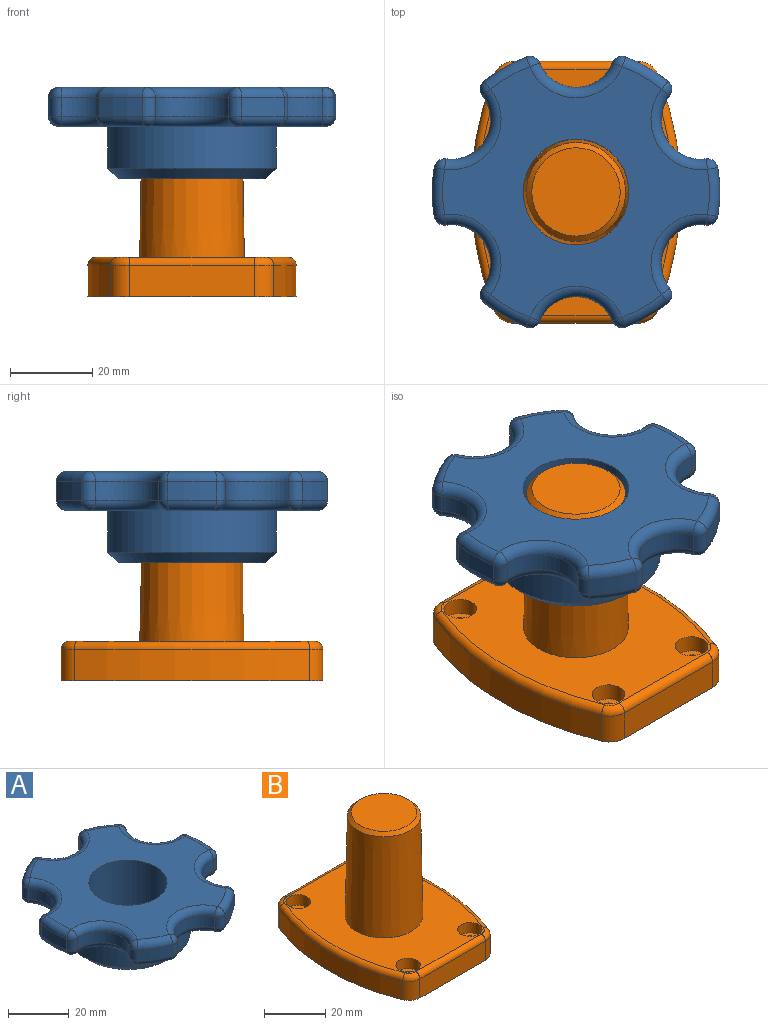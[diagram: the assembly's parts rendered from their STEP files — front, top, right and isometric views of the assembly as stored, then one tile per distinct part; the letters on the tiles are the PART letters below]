
ASSEMBLY  parts=2 mates=1
PART A: 78 faces, bbox 70.9x66.5x22.2 mm
  f0: plane 64.77x60.79mm, normal (0,0,1), area 1867.1mm2, adj f8,f30,f33,f34,f37,f38,f41,f42
  f1: cylinder r=34.92mm len=11.89mm, axis (0,0,-1), area 53.1mm2, adj f26,f28,f37,f61
  f2: cylinder r=34.92mm len=10.3mm, axis (0,0,-1), area 53.1mm2, adj f23,f25,f45,f69
  f3: cylinder r=34.92mm len=10.3mm, axis (0,0,-1), area 53.1mm2, adj f20,f22,f53,f77
  f4: cylinder r=34.92mm len=11.89mm, axis (0,0,-1), area 53.1mm2, adj f17,f19,f46,f70
  f5: cylinder r=34.92mm len=10.3mm, axis (0,0,-1), area 53.1mm2, adj f14,f16,f38,f62
  f6: plane 64.77x60.79mm, normal (0,0,-1), area 1070.6mm2, adj f10,f54,f57,f58,f61,f62,f65,f66
  f7: cylinder r=34.92mm len=10.3mm, axis (0,0,-1), area 53.1mm2, adj f13,f29,f30,f54
  f8: cylinder r=12.83mm len=25.65mm, axis (0,0,-1), area 1791.2mm2, adj f0,f9
  f9: plane 35.81x35.81mm, normal (0,0,-1), area 490.5mm2, adj f8,f11
  f10: cylinder r=20.45mm len=40.89mm, axis (0,0,-1), area 1305.3mm2, adj f6,f11
  f11: cone r=17.91mm half-angle=45deg, axis (0,0,1), area 432.8mm2, adj f9,f10
  f12: cylinder r=9.53mm len=17.66mm, axis (0,0,1), area 100.4mm2, adj f13,f14,f34,f58
  f13: cylinder r=2.54mm len=4.45mm, axis (0,0,1), area 17.4mm2, adj f7,f12,f32,f56
  f14: cylinder r=2.54mm len=4.45mm, axis (0,0,-1), area 17.4mm2, adj f5,f12,f36,f60
  f15: cylinder r=9.53mm len=15.38mm, axis (0,0,1), area 100.4mm2, adj f16,f17,f42,f66
  f16: cylinder r=2.54mm len=4.45mm, axis (0,0,1), area 17.4mm2, adj f5,f15,f40,f64
  f17: cylinder r=2.54mm len=4.45mm, axis (0,0,-1), area 17.4mm2, adj f4,f15,f44,f68
  f18: cylinder r=9.53mm len=15.38mm, axis (0,0,1), area 100.4mm2, adj f19,f20,f50,f74
  f19: cylinder r=2.54mm len=4.45mm, axis (0,0,1), area 17.4mm2, adj f4,f18,f48,f72
  f20: cylinder r=2.54mm len=4.45mm, axis (0,0,-1), area 17.4mm2, adj f3,f18,f52,f76
  f21: cylinder r=9.53mm len=17.66mm, axis (0,0,1), area 100.4mm2, adj f22,f23,f49,f73
  f22: cylinder r=2.54mm len=4.45mm, axis (0,0,1), area 17.4mm2, adj f3,f21,f51,f75
  f23: cylinder r=2.54mm len=4.45mm, axis (0,0,-1), area 17.4mm2, adj f2,f21,f47,f71
  f24: cylinder r=9.53mm len=15.38mm, axis (0,0,1), area 100.4mm2, adj f25,f26,f41,f65
  f25: cylinder r=2.54mm len=4.45mm, axis (0,0,1), area 17.4mm2, adj f2,f24,f43,f67
  f26: cylinder r=2.54mm len=4.45mm, axis (0,0,-1), area 17.4mm2, adj f1,f24,f39,f63
  f27: cylinder r=9.53mm len=15.38mm, axis (0,0,1), area 100.4mm2, adj f28,f29,f33,f57
  f28: cylinder r=2.54mm len=4.45mm, axis (0,0,1), area 17.4mm2, adj f1,f27,f35,f59
  f29: cylinder r=2.54mm len=4.45mm, axis (0,0,-1), area 17.4mm2, adj f7,f27,f31,f55
  f30: torus R=32.38mm, axis (0,0,-1), area 46.4mm2, adj f0,f7,f31,f32
  f31: sphere r=2.54mm, area 9.9mm2, adj f29,f30,f33
  f32: sphere r=2.54mm, area 9.9mm2, adj f13,f30,f34
  f33: torus R=12.06mm, axis (0,0,-1), area 98.9mm2, adj f0,f27,f31,f35
  f34: torus R=12.06mm, axis (0,0,-1), area 98.9mm2, adj f0,f12,f32,f36
  f35: sphere r=2.54mm, area 9.9mm2, adj f28,f33,f37
  f36: sphere r=2.54mm, area 9.9mm2, adj f14,f34,f38
  f37: torus R=32.38mm, axis (0,0,-1), area 46.4mm2, adj f0,f1,f35,f39
  f38: torus R=32.38mm, axis (0,0,-1), area 46.4mm2, adj f0,f5,f36,f40
  f39: sphere r=2.54mm, area 9.9mm2, adj f26,f37,f41
  f40: sphere r=2.54mm, area 9.9mm2, adj f16,f38,f42
  f41: torus R=12.06mm, axis (0,0,-1), area 98.9mm2, adj f0,f24,f39,f43
  f42: torus R=12.06mm, axis (0,0,-1), area 98.9mm2, adj f0,f15,f40,f44
  f43: sphere r=2.54mm, area 9.9mm2, adj f25,f41,f45
  f44: sphere r=2.54mm, area 9.9mm2, adj f17,f42,f46
  f45: torus R=32.38mm, axis (0,0,-1), area 46.4mm2, adj f0,f2,f43,f47
  f46: torus R=32.38mm, axis (0,0,-1), area 46.4mm2, adj f0,f4,f44,f48
  f47: sphere r=2.54mm, area 9.9mm2, adj f23,f45,f49
  f48: sphere r=2.54mm, area 9.9mm2, adj f19,f46,f50
  f49: torus R=12.06mm, axis (0,0,-1), area 98.9mm2, adj f0,f21,f47,f51
  f50: torus R=12.06mm, axis (0,0,-1), area 98.9mm2, adj f0,f18,f48,f52
  f51: sphere r=2.54mm, area 9.9mm2, adj f22,f49,f53
  f52: sphere r=2.54mm, area 9.9mm2, adj f20,f50,f53
  f53: torus R=32.38mm, axis (0,0,-1), area 46.4mm2, adj f0,f3,f51,f52
  f54: torus R=32.38mm, axis (0,0,-1), area 46.4mm2, adj f6,f7,f55,f56
  f55: sphere r=2.54mm, area 9.9mm2, adj f29,f54,f57
  f56: sphere r=2.54mm, area 9.9mm2, adj f13,f54,f58
  f57: torus R=12.06mm, axis (0,0,-1), area 98.9mm2, adj f6,f27,f55,f59
  f58: torus R=12.06mm, axis (0,0,-1), area 98.9mm2, adj f6,f12,f56,f60
  f59: sphere r=2.54mm, area 9.9mm2, adj f28,f57,f61
  f60: sphere r=2.54mm, area 9.9mm2, adj f14,f58,f62
  f61: torus R=32.38mm, axis (0,0,-1), area 46.4mm2, adj f1,f6,f59,f63
  f62: torus R=32.38mm, axis (0,0,-1), area 46.4mm2, adj f5,f6,f60,f64
  f63: sphere r=2.54mm, area 9.9mm2, adj f26,f61,f65
  f64: sphere r=2.54mm, area 9.9mm2, adj f16,f62,f66
  f65: torus R=12.06mm, axis (0,0,-1), area 98.9mm2, adj f6,f24,f63,f67
  f66: torus R=12.06mm, axis (0,0,-1), area 98.9mm2, adj f6,f15,f64,f68
  f67: sphere r=2.54mm, area 9.9mm2, adj f25,f65,f69
  f68: sphere r=2.54mm, area 9.9mm2, adj f17,f66,f70
  f69: torus R=32.38mm, axis (0,0,-1), area 46.4mm2, adj f2,f6,f67,f71
  f70: torus R=32.38mm, axis (0,0,-1), area 46.4mm2, adj f4,f6,f68,f72
  f71: sphere r=2.54mm, area 9.9mm2, adj f23,f69,f73
  f72: sphere r=2.54mm, area 9.9mm2, adj f19,f70,f74
  f73: torus R=12.06mm, axis (0,0,-1), area 98.9mm2, adj f6,f21,f71,f75
  f74: torus R=12.06mm, axis (0,0,-1), area 98.9mm2, adj f6,f18,f72,f76
  f75: sphere r=2.54mm, area 9.9mm2, adj f22,f73,f77
  f76: sphere r=2.54mm, area 9.9mm2, adj f20,f74,f77
  f77: torus R=32.38mm, axis (0,0,-1), area 46.4mm2, adj f3,f6,f75,f76
PART B: 52 faces, bbox 63.4x64.3x50.8 mm
  f0: cone r=12.7mm half-angle=1deg, axis (0,0,-1), area 3105mm2, adj f5,f32
  f1: plane 21.42x21.42mm, normal (0,0,1), area 360.3mm2, adj f32
  f2: plane 30.26x7.62mm, normal (0,-1,0), area 230.6mm2, adj f7,f21,f23,f31
  f3: plane 30.26x7.62mm, normal (0,1,0), area 230.6mm2, adj f7,f20,f22,f24
  f4: cylinder r=76.2mm len=57.15mm, axis (0,0,-1), area 446.4mm2, adj f7,f22,f23,f28
  f5: plane 59.69x46.99mm, normal (0,0,1), area 1852.3mm2, adj f0,f10,f13,f16,f19,f24,f25,f26
  f6: cylinder r=76.2mm len=57.15mm, axis (0,0,-1), area 446.4mm2, adj f7,f20,f21,f27
  f7: plane 63.5x50.8mm, normal (0,0,-1), area 683.3mm2, adj f2,f3,f4,f6,f8,f11,f14,f17
  f8: cylinder r=2.25mm len=5.36mm, axis (0,0,1), area 75.7mm2, adj f7,f9
  f9: plane 7.94x7.94mm, normal (0,0,1), area 33.6mm2, adj f8,f10
  f10: cylinder r=3.97mm len=7.94mm, axis (0,0,1), area 103.9mm2, adj f5,f9
  f11: cylinder r=2.25mm len=5.36mm, axis (0,0,1), area 75.7mm2, adj f7,f12
  f12: plane 7.94x7.94mm, normal (0,0,1), area 33.6mm2, adj f11,f13
  f13: cylinder r=3.97mm len=7.94mm, axis (0,0,1), area 103.9mm2, adj f5,f12
  f14: cylinder r=2.25mm len=5.36mm, axis (0,0,1), area 75.7mm2, adj f7,f15
  f15: plane 7.94x7.94mm, normal (0,0,1), area 33.6mm2, adj f14,f16
  f16: cylinder r=3.97mm len=7.94mm, axis (0,0,1), area 103.9mm2, adj f5,f15
  f17: cylinder r=2.25mm len=5.36mm, axis (0,0,1), area 75.7mm2, adj f7,f18
  f18: plane 7.94x7.94mm, normal (0,0,1), area 33.6mm2, adj f17,f19
  f19: cylinder r=3.97mm len=7.94mm, axis (0,0,1), area 103.9mm2, adj f5,f18
  f20: cylinder r=5.08mm len=7.62mm, axis (0,0,-1), area 45.9mm2, adj f3,f6,f7,f25
  f21: cylinder r=5.08mm len=7.62mm, axis (0,0,-1), area 45.9mm2, adj f2,f6,f7,f29
  f22: cylinder r=5.08mm len=7.62mm, axis (0,0,-1), area 45.9mm2, adj f3,f4,f7,f26
  f23: cylinder r=5.08mm len=7.62mm, axis (0,0,-1), area 45.9mm2, adj f2,f4,f7,f30
  f24: cylinder r=1.91mm len=30.26mm, axis (1,0,0), area 90.5mm2, adj f3,f5,f25,f26
  f25: torus R=3.17mm, axis (0,0,1), area 15.6mm2, adj f5,f20,f24,f27
  f26: torus R=3.17mm, axis (0,0,1), area 15.6mm2, adj f5,f22,f24,f28
  f27: torus R=74.3mm, axis (0,0,1), area 173.7mm2, adj f5,f6,f25,f29
  f28: torus R=74.3mm, axis (0,0,1), area 173.7mm2, adj f4,f5,f26,f30
  f29: torus R=3.17mm, axis (0,0,1), area 15.6mm2, adj f5,f21,f27,f31
  f30: torus R=3.17mm, axis (0,0,1), area 15.6mm2, adj f5,f23,f28,f31
  f31: cylinder r=1.91mm len=30.26mm, axis (-1,0,0), area 90.5mm2, adj f2,f5,f29,f30
  f32: cone r=12mm half-angle=45.5deg, axis (0,0,-1), area 129.3mm2, adj f0,f1
  f33: plane 18.97x18.97mm, normal (0,0,-1), area 282.5mm2, adj f37
  f34: plane 22.78x6.99mm, normal (0,-1,0), area 139.3mm2, adj f7,f40,f42,f43,f44,f49,f50,f51
  f35: plane 11.83x10.32mm, normal (0,0,-1), area 33mm2, adj f38,f41,f47,f48
  f36: plane 11.83x10.32mm, normal (0,0,-1), area 33mm2, adj f38,f39,f45,f46
  f37: cone r=10.16mm half-angle=1deg, axis (0,0,-1), area 2553.2mm2, adj f33,f40
  f38: plane 22.78x6.99mm, normal (0,1,0), area 139.3mm2, adj f7,f35,f36,f40,f45,f46,f47,f48
  f39: cylinder r=73.66mm len=47.92mm, axis (0,0,-1), area 320.7mm2, adj f7,f36,f40,f42,f43,f44,f45,f46
  f40: plane 58.42x45.72mm, normal (0,0,-1), area 1724.1mm2, adj f34,f37,f38,f39,f41,f44,f46,f48
  f41: cylinder r=73.66mm len=47.92mm, axis (0,0,-1), area 320.7mm2, adj f7,f35,f40,f47,f48,f49,f50,f51
  f42: cylinder r=4.79mm len=9.35mm, axis (0,0,1), area 50.7mm2, adj f7,f34,f39,f43
  f43: plane 11.83x10.32mm, normal (0,0,-1), area 33mm2, adj f34,f39,f42,f44
  f44: cylinder r=6.51mm len=11.83mm, axis (0,0,1), area 85.5mm2, adj f34,f39,f40,f43
  f45: cylinder r=4.79mm len=9.35mm, axis (0,0,1), area 50.7mm2, adj f7,f36,f38,f39
  f46: cylinder r=6.51mm len=11.83mm, axis (0,0,1), area 85.5mm2, adj f36,f38,f39,f40
  f47: cylinder r=4.79mm len=9.35mm, axis (0,0,1), area 50.7mm2, adj f7,f35,f38,f41
  f48: cylinder r=6.51mm len=11.83mm, axis (0,0,1), area 85.5mm2, adj f35,f38,f40,f41
  f49: cylinder r=4.79mm len=9.35mm, axis (0,0,1), area 50.7mm2, adj f7,f34,f41,f50
  f50: plane 11.83x10.32mm, normal (0,0,-1), area 33mm2, adj f34,f41,f49,f51
  f51: cylinder r=6.51mm len=11.83mm, axis (0,0,1), area 85.5mm2, adj f34,f40,f41,f50
PLACE A rot(axis=(0,0,1),0deg) t=(-0.34,13.01,22.98)mm
PLACE B t=(-0.34,13.01,-5.59)mm fixed
MATE cylindrical A.f1 <-> B.f0  axis (0,0,-1) through (-0.34,13.01,45.21)mm
